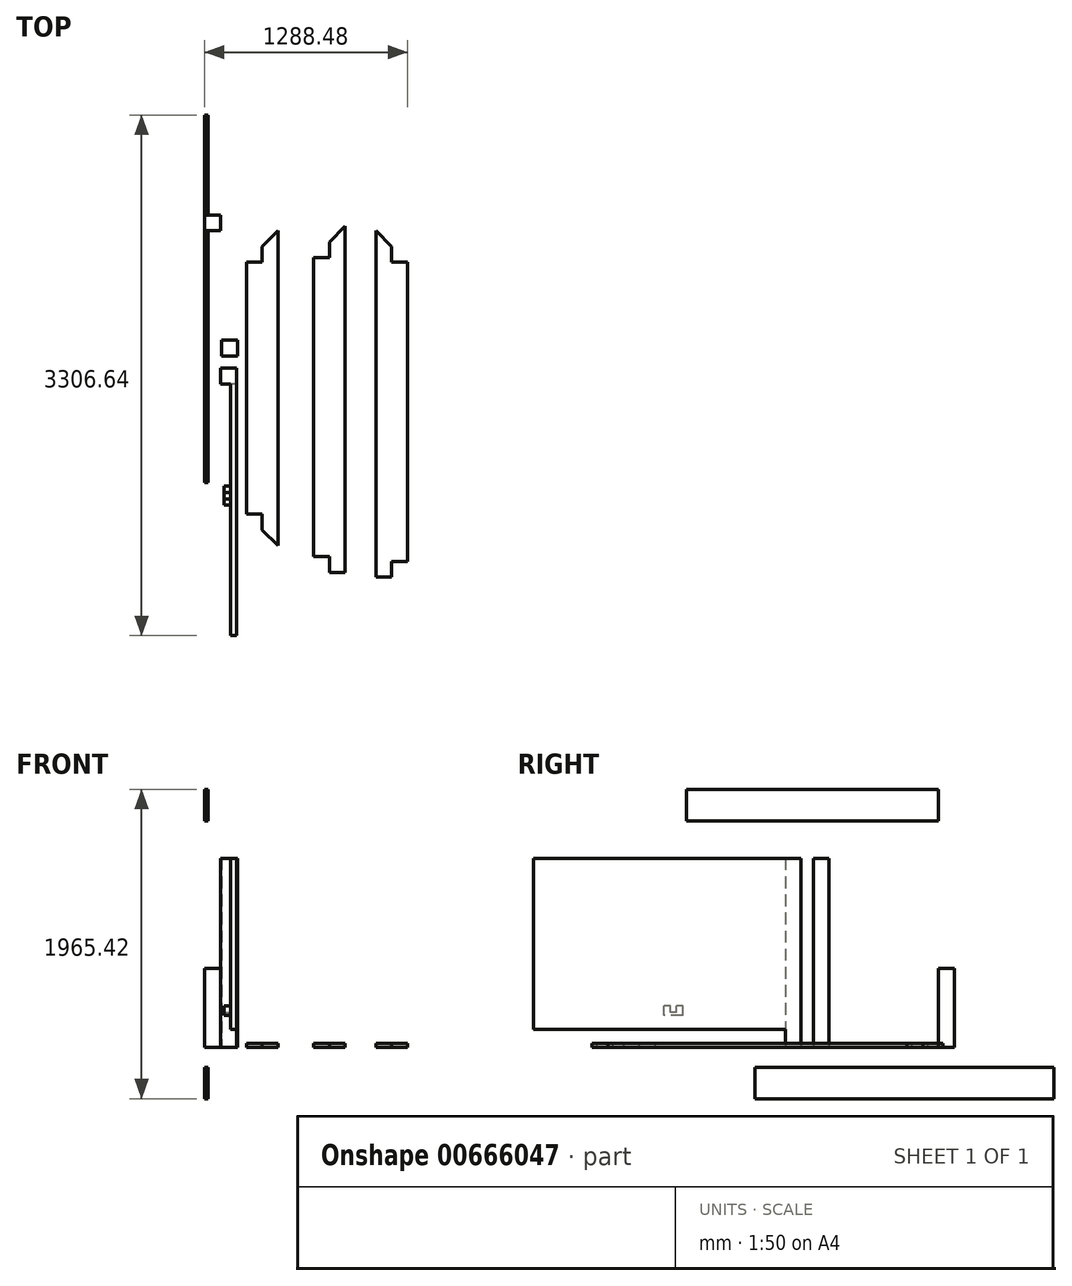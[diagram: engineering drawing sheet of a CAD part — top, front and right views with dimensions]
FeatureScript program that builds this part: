
annotation { "Feature Type Name" : "Feature", "Feature Type Description" : "" }
export const myFeature = defineFeature(function(context is Context, id is Id, definition is map)
    precondition{}
    {
        {
            var Q0;
            Q0=qCreatedBy(makeId("Top.planeOp"),FACE);
            var sketch = newSketch(context, id + "F0", { "sketchPlane" : qUnion([Q0])});
            skLineSegment(sketch, "E0.bottom", {"start": v(0, 0) * mm, "end": v(100, 0) * mm});
            skLineSegment(sketch, "E0.top", {"start": v(0, 100) * mm, "end": v(100, 100) * mm});
            skLineSegment(sketch, "E0.left", {"start": v(0, 0) * mm, "end": v(0, 100) * mm});
            skLineSegment(sketch, "E0.right", {"start": v(100, 0) * mm, "end": v(100, 100) * mm});
            skSolve(sketch);
        }
        {
            var Q0;
            Q0=makeQuery(id+"F0.imprint","IMPRINT",FACE,{"disambiguationData":[TD([[makeQuery(id+"F0.imprint","IMPRINT",EDGE,{"derivedFrom":sQuery(id+"F0.wireOp",EDGE,"E0.bottom")}),1.0]])]});
            extrude(context, id + "F1", {"entities" : qUnion([Q0]), "depth" : 500 * mm, "offsetDistance" : 25.4 * mm});
        }
        {
            var Q0;
            Q0=qCreatedBy(makeId("Right.planeOp"),FACE);
            var sketch = newSketch(context, id + "F2", { "sketchPlane" : qUnion([Q0])});
            skLineSegment(sketch, "E1.bottom", {"start": v(0, 1438.56) * mm, "end": v(-1600, 1438.56) * mm});
            skLineSegment(sketch, "E1.top", {"start": v(0, 1638.56) * mm, "end": v(-1600, 1638.56) * mm});
            skLineSegment(sketch, "E1.left", {"start": v(0, 1438.56) * mm, "end": v(0, 1638.56) * mm});
            skLineSegment(sketch, "E1.right", {"start": v(-1600, 1438.56) * mm, "end": v(-1600, 1638.56) * mm});
            skSolve(sketch);
        }
        {
            var Q0;
            Q0=makeQuery(id+"F2.imprint","IMPRINT",FACE,{"disambiguationData":[TD([[makeQuery(id+"F2.imprint","IMPRINT",EDGE,{"derivedFrom":sQuery(id+"F2.wireOp",EDGE,"E1.bottom")}),-1.0]])]});
            extrude(context, id + "F3", {"entities" : qUnion([Q0]), "depth" : 23 * mm, "offsetDistance" : 25.4 * mm});
        }
        {
            var Q0;
            Q0=qCreatedBy(makeId("Top.planeOp"),FACE);
            var sketch = newSketch(context, id + "F4", { "sketchPlane" : qUnion([Q0])});
            skLineSegment(sketch, "E2", {"start": v(265.56, -200) * mm, "end": v(265.56, -1800) * mm});
            skLineSegment(sketch, "E3", {"start": v(265.56, -1800) * mm, "end": v(465.56, -2000) * mm});
            skLineSegment(sketch, "E4", {"start": v(465.56, -2000) * mm, "end": v(465.56, 0) * mm});
            skLineSegment(sketch, "E5", {"start": v(465.56, 0) * mm, "end": v(265.56, -200) * mm});
            skSolve(sketch);
        }
        {
            var Q0;
            Q0=makeQuery(id+"F4.imprint","IMPRINT",FACE,{"disambiguationData":[TD([[makeQuery(id+"F4.imprint","IMPRINT",EDGE,{"derivedFrom":sQuery(id+"F4.wireOp",EDGE,"E2")}),1.0]])]});
            extrude(context, id + "F5", {"entities" : qUnion([Q0]), "depth" : 23 * mm, "offsetDistance" : 25.4 * mm});
        }
        {
            var Q0;
            Q0=makeQuery(id+"F5.opExtrude","CAP_FACE",FACE,{"disambiguationData":[OSD([sQuery(id+"F4.wireOp",EDGE,"E2"),sQuery(id+"F4.wireOp",EDGE,"E3"),sQuery(id+"F4.wireOp",EDGE,"E4"),sQuery(id+"F4.wireOp",EDGE,"E5")])],"isStart":false});
            var sketch = newSketch(context, id + "F6", { "sketchPlane" : qUnion([Q0])});
            skLineSegment(sketch, "E6.bottom", {"start": v(265.56, -1800) * mm, "end": v(365.56, -1800) * mm});
            skLineSegment(sketch, "E6.top", {"start": v(265.56, -1900) * mm, "end": v(365.56, -1900) * mm});
            skLineSegment(sketch, "E6.left", {"start": v(265.56, -1800) * mm, "end": v(265.56, -1900) * mm});
            skLineSegment(sketch, "E6.right", {"start": v(365.56, -1800) * mm, "end": v(365.56, -1900) * mm});
            skSolve(sketch);
        }
        {
            var Q0;
            {var subQ0=sQuery(id+"F6.wireOp",EDGE,"E6.bottom");Q0=makeQuery(id+"F6.imprint","IMPRINT",FACE,{"disambiguationData":[TD([[makeQuery(id+"F6.imprint","IMPRINT",EDGE,{"derivedFrom":subQ0}),-1.0]])]});}
            extrude(context, id + "F7", {"entities" : qUnion([Q0]), "operationType" : NewBodyOperationType.REMOVE, "oppositeDirection" : true, "depth" : 23 * mm, "offsetDistance" : 25.4 * mm});
        }
        {
            var Q0;
            Q0=makeQuery(id+"F5.opExtrude","CAP_FACE",FACE,{"disambiguationData":[OSD([sQuery(id+"F4.wireOp",EDGE,"E2"),sQuery(id+"F4.wireOp",EDGE,"E3"),sQuery(id+"F4.wireOp",EDGE,"E4"),sQuery(id+"F4.wireOp",EDGE,"E5")])],"isStart":false});
            var sketch = newSketch(context, id + "F8", { "sketchPlane" : qUnion([Q0])});
            skLineSegment(sketch, "E7.bottom", {"start": v(265.56, -200) * mm, "end": v(365.56, -200) * mm});
            skLineSegment(sketch, "E7.top", {"start": v(265.56, -100) * mm, "end": v(365.56, -100) * mm});
            skLineSegment(sketch, "E7.left", {"start": v(265.56, -200) * mm, "end": v(265.56, -100) * mm});
            skLineSegment(sketch, "E7.right", {"start": v(365.56, -200) * mm, "end": v(365.56, -100) * mm});
            skSolve(sketch);
        }
        {
            var Q0;
            {var subQ0=sQuery(id+"F8.wireOp",EDGE,"E7.bottom");Q0=makeQuery(id+"F8.imprint","IMPRINT",FACE,{"disambiguationData":[TD([[makeQuery(id+"F8.imprint","IMPRINT",EDGE,{"derivedFrom":subQ0}),1.0]])]});}
            extrude(context, id + "F9", {"entities" : qUnion([Q0]), "operationType" : NewBodyOperationType.REMOVE, "oppositeDirection" : true, "depth" : 23 * mm, "offsetDistance" : 25.4 * mm});
        }
        {
            var Q0;
            Q0=qCreatedBy(makeId("Top.planeOp"),FACE);
            var sketch = newSketch(context, id + "F10", { "sketchPlane" : qUnion([Q0])});
            skLineSegment(sketch, "E8.bottom", {"start": v(101.48, -872.36) * mm, "end": v(201.48, -872.36) * mm});
            skLineSegment(sketch, "E8.top", {"start": v(101.48, -972.36) * mm, "end": v(201.48, -972.36) * mm});
            skLineSegment(sketch, "E8.left", {"start": v(101.48, -872.36) * mm, "end": v(101.48, -972.36) * mm});
            skLineSegment(sketch, "E8.right", {"start": v(201.48, -872.36) * mm, "end": v(201.48, -972.36) * mm});
            skSolve(sketch);
        }
        {
            var Q0;
            Q0=makeQuery(id+"F10.imprint","IMPRINT",FACE,{"disambiguationData":[TD([[makeQuery(id+"F10.imprint","IMPRINT",EDGE,{"derivedFrom":sQuery(id+"F10.wireOp",EDGE,"E8.bottom")}),-1.0]])]});
            extrude(context, id + "F11", {"entities" : qUnion([Q0]), "depth" : 1200 * mm, "offsetDistance" : 25.4 * mm});
        }
        {
            var Q0;
            Q0=makeQuery(id+"F11.opExtrude","SWEPT_FACE",FACE,{"disambiguationData":[OSD([sQuery(id+"F10.wireOp",EDGE,"E8.top")])]});
            var sketch = newSketch(context, id + "F12", { "sketchPlane" : qUnion([Q0])});
            skLineSegment(sketch, "E9.bottom", {"start": v(201.48, 1200) * mm, "end": v(165.01, 1200) * mm});
            skLineSegment(sketch, "E9.top", {"start": v(201.48, 112.71) * mm, "end": v(165.01, 112.71) * mm});
            skLineSegment(sketch, "E9.left", {"start": v(201.48, 1200) * mm, "end": v(201.48, 112.71) * mm});
            skLineSegment(sketch, "E9.right", {"start": v(165.01, 1200) * mm, "end": v(165.01, 112.71) * mm});
            skSolve(sketch);
        }
        {
            var Q0;
            Q0=makeQuery(id+"F12.imprint","IMPRINT",FACE,{"disambiguationData":[TD([[makeQuery(id+"F12.imprint","IMPRINT",EDGE,{"derivedFrom":sQuery(id+"F12.wireOp",EDGE,"E9.bottom")}),-1.0]])]});
            extrude(context, id + "F13", {"entities" : qUnion([Q0]), "operationType" : NewBodyOperationType.ADD, "depth" : 1600 * mm, "offsetDistance" : 25.4 * mm});
        }
        {
            var Q0;
            Q0=makeQuery(id+"F13.opExtrude","SWEPT_FACE",FACE,{"disambiguationData":[OSD([sQuery(id+"F12.wireOp",EDGE,"E9.right")])]});
            var sketch = newSketch(context, id + "F14", { "sketchPlane" : qUnion([Q0])});
            skLineSegment(sketch, "E10.bottom", {"start": v(1622.93, 201.38) * mm, "end": v(1742.93, 201.38) * mm});
            skLineSegment(sketch, "E10.top", {"start": v(1622.93, 261.38) * mm, "end": v(1742.93, 261.38) * mm});
            skLineSegment(sketch, "E10.left", {"start": v(1622.93, 201.38) * mm, "end": v(1622.93, 261.38) * mm});
            skLineSegment(sketch, "E10.right", {"start": v(1742.93, 201.38) * mm, "end": v(1742.93, 261.38) * mm});
            skSolve(sketch);
        }
        {
            var Q0;
            Q0=makeQuery(id+"F14.imprint","IMPRINT",FACE,{"disambiguationData":[TD([[makeQuery(id+"F14.imprint","IMPRINT",EDGE,{"derivedFrom":sQuery(id+"F14.wireOp",EDGE,"E10.bottom")}),1.0]])]});
            extrude(context, id + "F15", {"entities" : qUnion([Q0]), "operationType" : NewBodyOperationType.ADD, "depth" : 40 * mm, "offsetDistance" : 25.4 * mm});
        }
        {
            var Q0;
            Q0=makeQuery(id+"F15.opExtrude","SWEPT_FACE",FACE,{"disambiguationData":[OSD([sQuery(id+"F14.wireOp",EDGE,"E10.top")])]});
            var sketch = newSketch(context, id + "F16", { "sketchPlane" : qUnion([Q0])});
            skLineSegment(sketch, "E11.bottom", {"start": v(125.01, -1702.93) * mm, "end": v(165.01, -1702.93) * mm});
            skLineSegment(sketch, "E11.top", {"start": v(125.01, -1662.93) * mm, "end": v(165.01, -1662.93) * mm});
            skLineSegment(sketch, "E11.left", {"start": v(125.01, -1702.93) * mm, "end": v(125.01, -1662.93) * mm});
            skLineSegment(sketch, "E11.right", {"start": v(165.01, -1702.93) * mm, "end": v(165.01, -1662.93) * mm});
            skPoint(sketch, "E11.middle", {"position": v(145.01, -1682.93) * mm});
            skPoint(sketch, "E11.middle.positionSnap0", {"position": v(145.01, -1742.93) * mm});
            skPoint(sketch, "E11.middle.positionSnap1", {"position": v(125.01, -1682.93) * mm});
            skPoint(sketch, "E11.centerSnap0", {"position": v(145.01, -1742.93) * mm});
            skPoint(sketch, "E11.centerSnap1", {"position": v(125.01, -1682.93) * mm});
            skSolve(sketch);
        }
        {
            var Q0;
            Q0=makeQuery(id+"F16.imprint","IMPRINT",FACE,{"disambiguationData":[TD([[makeQuery(id+"F16.imprint","IMPRINT",EDGE,{"derivedFrom":sQuery(id+"F16.wireOp",EDGE,"E11.bottom")}),1.0]])]});
            extrude(context, id + "F17", {"entities" : qUnion([Q0]), "operationType" : NewBodyOperationType.REMOVE, "oppositeDirection" : true, "depth" : 40 * mm, "offsetDistance" : 25.4 * mm});
        }
        {
            var Q0;
            Q0=qCreatedBy(makeId("Right.planeOp"),FACE);
            var sketch = newSketch(context, id + "F18", { "sketchPlane" : qUnion([Q0])});
            skLineSegment(sketch, "E12.bottom", {"start": v(734.28, -126.86) * mm, "end": v(-1165.72, -126.86) * mm});
            skLineSegment(sketch, "E12.top", {"start": v(734.28, -326.86) * mm, "end": v(-1165.72, -326.86) * mm});
            skLineSegment(sketch, "E12.left", {"start": v(734.28, -126.86) * mm, "end": v(734.28, -326.86) * mm});
            skLineSegment(sketch, "E12.right", {"start": v(-1165.72, -126.86) * mm, "end": v(-1165.72, -326.86) * mm});
            skSolve(sketch);
        }
        {
            var Q0;
            Q0=makeQuery(id+"F18.imprint","IMPRINT",FACE,{"disambiguationData":[TD([[makeQuery(id+"F18.imprint","IMPRINT",EDGE,{"derivedFrom":sQuery(id+"F18.wireOp",EDGE,"E12.bottom")}),1.0]])]});
            extrude(context, id + "F19", {"entities" : qUnion([Q0]), "depth" : 23 * mm, "offsetDistance" : 25.4 * mm});
        }
        {
            var Q0;
            Q0=qCreatedBy(makeId("Top.planeOp"),FACE);
            var sketch = newSketch(context, id + "F20", { "sketchPlane" : qUnion([Q0])});
            skLineSegment(sketch, "E13", {"start": v(693.06, -170.73) * mm, "end": v(793.06, -170.73) * mm});
            skLineSegment(sketch, "E14", {"start": v(793.06, -170.73) * mm, "end": v(793.06, -70.73) * mm});
            skLineSegment(sketch, "E15", {"start": v(793.06, -70.73) * mm, "end": v(893.06, 29.27) * mm});
            skLineSegment(sketch, "E16", {"start": v(893.06, 29.27) * mm, "end": v(893.06, -2170.73) * mm});
            skLineSegment(sketch, "E17", {"start": v(893.06, -2170.73) * mm, "end": v(793.06, -2170.73) * mm});
            skLineSegment(sketch, "E18", {"start": v(793.06, -2170.73) * mm, "end": v(793.06, -2070.73) * mm});
            skLineSegment(sketch, "E19", {"start": v(793.06, -2070.73) * mm, "end": v(693.06, -2070.73) * mm});
            skLineSegment(sketch, "E20", {"start": v(693.06, -2070.73) * mm, "end": v(693.06, -170.73) * mm});
            skSolve(sketch);
        }
        {
            var Q0;
            Q0=makeQuery(id+"F20.imprint","IMPRINT",FACE,{"disambiguationData":[TD([[makeQuery(id+"F20.imprint","IMPRINT",EDGE,{"derivedFrom":sQuery(id+"F20.wireOp",EDGE,"E13")}),-1.0]])]});
            extrude(context, id + "F21", {"entities" : qUnion([Q0]), "depth" : 23 * mm, "offsetDistance" : 25.4 * mm});
        }
        {
            var Q0;
            Q0=qCreatedBy(makeId("Top.planeOp"),FACE);
            var sketch = newSketch(context, id + "F22", { "sketchPlane" : qUnion([Q0])});
            skLineSegment(sketch, "E21", {"start": v(1088.48, 0) * mm, "end": v(1088.48, -2200) * mm});
            skLineSegment(sketch, "E22", {"start": v(1088.48, -2200) * mm, "end": v(1188.48, -2200) * mm});
            skLineSegment(sketch, "E23", {"start": v(1188.48, -2200) * mm, "end": v(1188.48, -2100) * mm});
            skLineSegment(sketch, "E24", {"start": v(1188.48, -2100) * mm, "end": v(1288.48, -2100) * mm});
            skLineSegment(sketch, "E25", {"start": v(1288.48, -2100) * mm, "end": v(1288.48, -200) * mm});
            skLineSegment(sketch, "E26", {"start": v(1288.48, -200) * mm, "end": v(1188.48, -200) * mm});
            skLineSegment(sketch, "E27", {"start": v(1188.48, -200) * mm, "end": v(1188.48, -100) * mm});
            skLineSegment(sketch, "E28", {"start": v(1188.48, -100) * mm, "end": v(1088.48, 0) * mm});
            skSolve(sketch);
        }
        {
            var Q0;
            Q0=makeQuery(id+"F22.imprint","IMPRINT",FACE,{"disambiguationData":[TD([[makeQuery(id+"F22.imprint","IMPRINT",EDGE,{"derivedFrom":sQuery(id+"F22.wireOp",EDGE,"E21")}),1.0]])]});
            extrude(context, id + "F23", {"entities" : qUnion([Q0]), "depth" : 23 * mm, "offsetDistance" : 25.4 * mm});
        }
        {
            var Q0;
            Q0=qCreatedBy(makeId("Top.planeOp"),FACE);
            var sketch = newSketch(context, id + "F24", { "sketchPlane" : qUnion([Q0])});
            skLineSegment(sketch, "E29.bottom", {"start": v(109.28, -795.23) * mm, "end": v(209.28, -795.23) * mm});
            skLineSegment(sketch, "E29.top", {"start": v(109.28, -695.23) * mm, "end": v(209.28, -695.23) * mm});
            skLineSegment(sketch, "E29.left", {"start": v(109.28, -795.23) * mm, "end": v(109.28, -695.23) * mm});
            skLineSegment(sketch, "E29.right", {"start": v(209.28, -795.23) * mm, "end": v(209.28, -695.23) * mm});
            skSolve(sketch);
        }
        {
            var Q0;
            Q0=makeQuery(id+"F24.imprint","IMPRINT",FACE,{"disambiguationData":[TD([[makeQuery(id+"F24.imprint","IMPRINT",EDGE,{"derivedFrom":sQuery(id+"F24.wireOp",EDGE,"E29.bottom")}),1.0]])]});
            extrude(context, id + "F25", {"entities" : qUnion([Q0]), "depth" : 1200 * mm, "offsetDistance" : 25.4 * mm});
        }
    });
